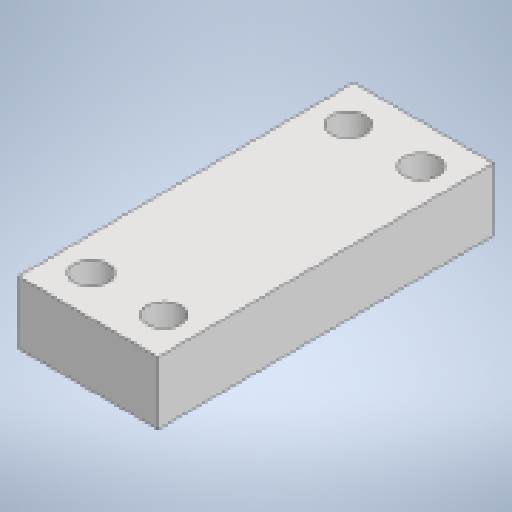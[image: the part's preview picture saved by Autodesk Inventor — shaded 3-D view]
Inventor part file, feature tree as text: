
AUTODESK INVENTOR PART (.ipt)
format: ipt  version: 2023 (Build 270158000, 158)  size: 141,312 bytes
history: native  units: mm
features: extrude x2, sketch x2, pattern_linear x1
ambient origin geometry x8: Origin, YZ Plane, XZ Plane, XY Plane, X Axis, Y Axis, Z Axis, Center Point
bodies: Solid1 (feature_tree)
feature tree (5):
  extrude  "Extrusion1"  Depth=11.2mm
  extrude  "Extrusion2"  Depth=25.0mm
  pattern_linear  "Rectangular Pattern1"  Spacing1=6.0mm  [1 undecoded]
  sketch  "Sketch1"  dims[d2=60.0mm d4=11.2mm]
  sketch  "Sketch2"  dims[d5=25.0mm d6=0.0mm d7=6.0mm d8=6.0mm d9=7.0mm d10=20.0mm d11=0.0mm d12=20.0mm d14=46.0mm d15=20.0mm d17=13.0mm]
note: 1 required parameter value undecoded (feature->parameter linkage not recoverable at this tier; creation-order binding heuristic only, values carry confidence <= 0.55)
